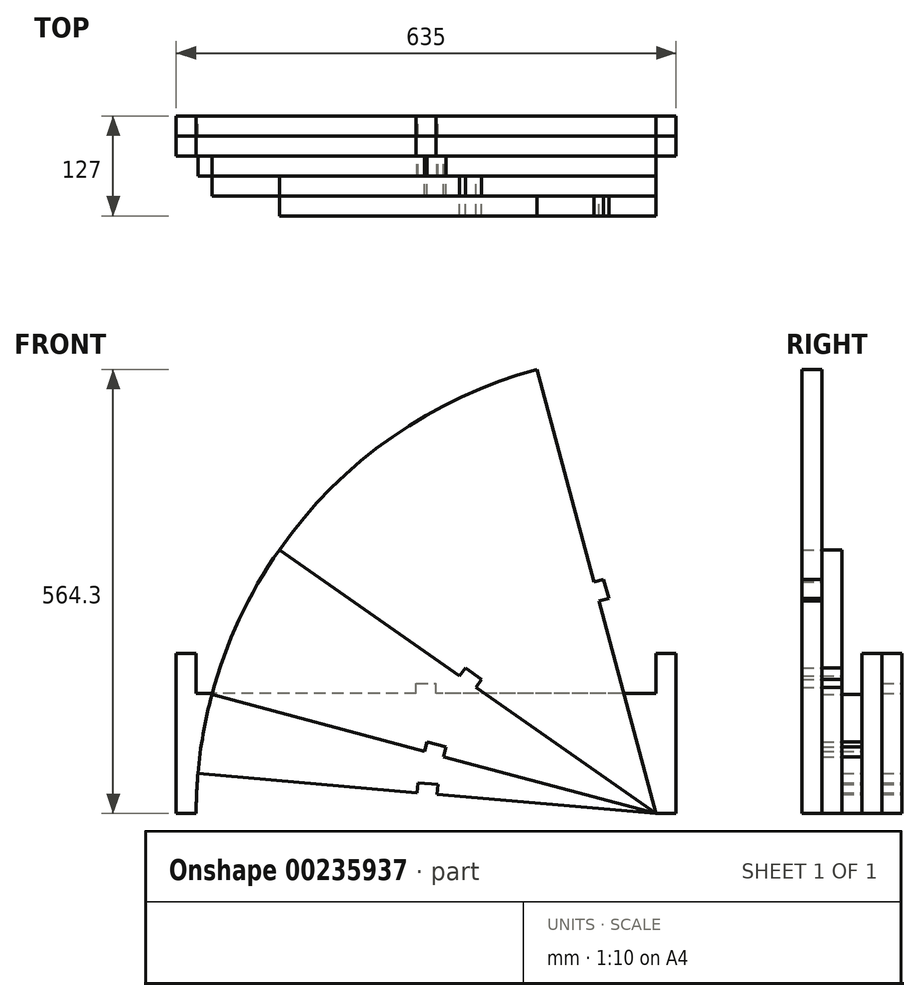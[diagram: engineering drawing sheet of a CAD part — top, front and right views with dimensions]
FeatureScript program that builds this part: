
annotation { "Feature Type Name" : "Feature", "Feature Type Description" : "" }
export const myFeature = defineFeature(function(context is Context, id is Id, definition is map)
    precondition{}
    {
        {
            var Q0;
            Q0=qCreatedBy(makeId("Front.planeOp"),FACE);
            var sketch = newSketch(context, id + "F0", { "sketchPlane" : qUnion([Q0])});
            skLineSegment(sketch, "E0", {"start": v(-127.48, -54.08) * mm, "end": v(177.32, -54.08) * mm});
            skLineSegment(sketch, "E1", {"start": v(507.52, -54.08) * mm, "end": v(507.52, 149.12) * mm});
            skLineSegment(sketch, "E2", {"start": v(507.52, 149.12) * mm, "end": v(482.12, 149.12) * mm});
            skLineSegment(sketch, "E3", {"start": v(482.12, 149.12) * mm, "end": v(482.12, 98.32) * mm});
            skLineSegment(sketch, "E4", {"start": v(482.12, 98.32) * mm, "end": v(202.72, 98.32) * mm});
            skLineSegment(sketch, "E5", {"start": v(-102.08, 98.32) * mm, "end": v(-102.08, 149.12) * mm});
            skLineSegment(sketch, "E6", {"start": v(-102.08, 149.12) * mm, "end": v(-127.48, 149.12) * mm});
            skLineSegment(sketch, "E7", {"start": v(-127.48, 149.12) * mm, "end": v(-127.48, -54.08) * mm});
            skPoint(sketch, "E8", {"position": v(190.02, 98.32) * mm});
            skPoint(sketch, "E9", {"position": v(202.72, 98.32) * mm});
            skPoint(sketch, "E10", {"position": v(177.32, 98.32) * mm});
            skLineSegment(sketch, "E11.top", {"start": v(177.32, 111.02) * mm, "end": v(202.72, 111.02) * mm});
            skLineSegment(sketch, "E11.left", {"start": v(177.32, 98.32) * mm, "end": v(177.32, 111.02) * mm});
            skLineSegment(sketch, "E11.right", {"start": v(202.72, 98.32) * mm, "end": v(202.72, 111.02) * mm});
            skLineSegment(sketch, "E12.trimOffspring", {"start": v(177.32, 98.32) * mm, "end": v(-102.08, 98.32) * mm});
            skArc(sketch, "E13", {"start": v(-102.08, -54.08) * mm, "mid": v(-101.52, -28.6) * mm, "end": v(-99.85, -3.16) * mm});
            skLineSegment(sketch, "E14", {"start": v(-99.85, -3.16) * mm, "end": v(178.48, -27.51) * mm});
            skLineSegment(sketch, "E15.top", {"start": v(202.72, -41.38) * mm, "end": v(177.32, -41.38) * mm});
            skLineSegment(sketch, "E15.left", {"start": v(202.72, -54.08) * mm, "end": v(202.72, -41.38) * mm});
            skLineSegment(sketch, "E15.right", {"start": v(177.32, -54.08) * mm, "end": v(177.32, -41.38) * mm});
            skLineSegment(sketch, "E16.trimOffspring", {"start": v(202.72, -54.08) * mm, "end": v(507.52, -54.08) * mm});
            skPoint(sketch, "E17", {"position": v(203.79, -29.73) * mm});
            skLineSegment(sketch, "E18", {"start": v(203.79, -29.73) * mm, "end": v(204.9, -17.07) * mm});
            skLineSegment(sketch, "E19", {"start": v(204.9, -17.07) * mm, "end": v(179.6, -14.86) * mm});
            skLineSegment(sketch, "E20", {"start": v(179.6, -14.86) * mm, "end": v(178.48, -27.51) * mm});
            skLineSegment(sketch, "E21.trimOffspring", {"start": v(203.79, -29.73) * mm, "end": v(482.12, -54.08) * mm});
            skSolve(sketch);
        }
        {
            var Q0;
            {var subQ4=sQuery(id+"F0.wireOp",EDGE,"E1");Q0=makeQuery(id+"F0.imprint","IMPRINT",FACE,{"disambiguationData":[TD([[makeQuery(id+"F0.imprint","IMPRINT",EDGE,{"derivedFrom":subQ4}),1.0]])]});}
            var Q1;
            {var subQ0=sQuery(id+"F0.wireOp",EDGE,"E13");Q1=makeQuery(id+"F0.imprint","IMPRINT",FACE,{"disambiguationData":[TD([[makeQuery(id+"F0.imprint","IMPRINT",EDGE,{"derivedFrom":subQ0}),-1.0]])]});}
            extrude(context, id + "F1", {"entities" : qUnion([Q0, Q1]), "depth" : 25.4 * mm});
        }
        {
            var Q0;
            {var subQ0=sQuery(id+"F0.wireOp",EDGE,"E13");Q0=makeQuery(id+"F0.imprint","IMPRINT",FACE,{"disambiguationData":[TD([[makeQuery(id+"F0.imprint","IMPRINT",EDGE,{"derivedFrom":subQ0}),-1.0]])]});}
            extrude(context, id + "F2", {"entities" : qUnion([Q0]), "depth" : 50.8 * mm});
        }
        {
            var Q0;
            Q0=makeQuery(id+"F2.opExtrude","CAP_FACE",FACE,{"disambiguationData":[OSD([sQuery(id+"F0.wireOp",EDGE,"E0"),sQuery(id+"F0.wireOp",EDGE,"E13"),sQuery(id+"F0.wireOp",EDGE,"E14"),sQuery(id+"F0.wireOp",EDGE,"E15.top"),sQuery(id+"F0.wireOp",EDGE,"E15.left"),sQuery(id+"F0.wireOp",EDGE,"E15.right"),sQuery(id+"F0.wireOp",EDGE,"E16.trimOffspring"),sQuery(id+"F0.wireOp",EDGE,"E18"),sQuery(id+"F0.wireOp",EDGE,"E19"),sQuery(id+"F0.wireOp",EDGE,"E20"),sQuery(id+"F0.wireOp",EDGE,"E21.trimOffspring")])],"isStart":false});
            var sketch = newSketch(context, id + "F3", { "sketchPlane" : qUnion([Q0])});
            skLineSegment(sketch, "E22.0", {"start": v(-99.85, -3.16) * mm, "end": v(178.48, -27.51) * mm});
            skLineSegment(sketch, "E23.0", {"start": v(203.79, -29.73) * mm, "end": v(482.12, -54.08) * mm});
            skLineSegment(sketch, "E24.0", {"start": v(204.9, -17.07) * mm, "end": v(179.6, -14.86) * mm});
            skLineSegment(sketch, "E25.0", {"start": v(179.6, -14.86) * mm, "end": v(178.48, -27.51) * mm});
            skLineSegment(sketch, "E26.0", {"start": v(203.79, -29.73) * mm, "end": v(204.9, -17.07) * mm});
            skArc(sketch, "E27", {"start": v(-99.85, -3.16) * mm, "mid": v(-93.2, 47.37) * mm, "end": v(-82.17, 97.13) * mm});
            skLineSegment(sketch, "E28", {"start": v(-82.17, 97.13) * mm, "end": v(187.71, 24.81) * mm});
            skPoint(sketch, "E29", {"position": v(212.25, 18.24) * mm});
            skLineSegment(sketch, "E30", {"start": v(212.25, 18.24) * mm, "end": v(215.53, 30.5) * mm});
            skLineSegment(sketch, "E31", {"start": v(215.53, 30.5) * mm, "end": v(191, 37.08) * mm});
            skLineSegment(sketch, "E32", {"start": v(191, 37.08) * mm, "end": v(187.71, 24.81) * mm});
            skLineSegment(sketch, "E33.trimOffspring", {"start": v(212.25, 18.24) * mm, "end": v(482.12, -54.08) * mm});
            skSolve(sketch);
        }
        {
            var Q0;
            Q0=makeQuery(id+"F3.imprint","IMPRINT",FACE,{"disambiguationData":[TD([[makeQuery(id+"F3.imprint","IMPRINT",EDGE,{"derivedFrom":sQuery(id+"F3.wireOp",EDGE,"E22.0")}),1.0]])]});
            extrude(context, id + "F4", {"entities" : qUnion([Q0]), "depth" : 25.4 * mm});
        }
        {
            var Q0;
            Q0=makeQuery(id+"F4.opExtrude","CAP_FACE",FACE,{"disambiguationData":[OSD([sQuery(id+"F3.wireOp",EDGE,"E22.0"),sQuery(id+"F3.wireOp",EDGE,"E23.0"),sQuery(id+"F3.wireOp",EDGE,"E24.0"),sQuery(id+"F3.wireOp",EDGE,"E25.0"),sQuery(id+"F3.wireOp",EDGE,"E26.0"),sQuery(id+"F3.wireOp",EDGE,"E27"),sQuery(id+"F3.wireOp",EDGE,"E28"),sQuery(id+"F3.wireOp",EDGE,"E30"),sQuery(id+"F3.wireOp",EDGE,"E31"),sQuery(id+"F3.wireOp",EDGE,"E32"),sQuery(id+"F3.wireOp",EDGE,"E33.trimOffspring")])],"isStart":false});
            var sketch = newSketch(context, id + "F5", { "sketchPlane" : qUnion([Q0])});
            skLineSegment(sketch, "E34.0", {"start": v(212.25, 18.24) * mm, "end": v(482.12, -54.08) * mm});
            skLineSegment(sketch, "E35.0", {"start": v(215.53, 30.5) * mm, "end": v(191, 37.08) * mm});
            skLineSegment(sketch, "E36.0", {"start": v(212.25, 18.24) * mm, "end": v(215.53, 30.5) * mm});
            skLineSegment(sketch, "E37.0", {"start": v(191, 37.08) * mm, "end": v(187.71, 24.81) * mm});
            skLineSegment(sketch, "E38.0", {"start": v(-82.17, 97.13) * mm, "end": v(187.71, 24.81) * mm});
            skArc(sketch, "E39", {"start": v(-82.17, 97.13) * mm, "mid": v(-47.34, 192.82) * mm, "end": v(3.58, 281) * mm});
            skLineSegment(sketch, "E40", {"start": v(3.58, 281) * mm, "end": v(232.45, 120.75) * mm});
            skPoint(sketch, "E41", {"position": v(253.25, 106.18) * mm});
            skPoint(sketch, "E42", {"position": v(232.45, 120.75) * mm});
            skLineSegment(sketch, "E43", {"start": v(253.25, 106.18) * mm, "end": v(260.54, 116.58) * mm});
            skLineSegment(sketch, "E44", {"start": v(232.45, 120.75) * mm, "end": v(239.73, 131.15) * mm});
            skLineSegment(sketch, "E45", {"start": v(239.73, 131.15) * mm, "end": v(260.54, 116.58) * mm});
            skLineSegment(sketch, "E46.trimOffspring", {"start": v(253.25, 106.18) * mm, "end": v(482.12, -54.08) * mm});
            skSolve(sketch);
        }
        {
            var Q0;
            Q0 = qSketchRegion(id + "F5", true);
            extrude(context, id + "F6", {"entities" : qUnion([Q0]), "depth" : 25.4 * mm});
        }
        {
            var Q0;
            Q0=makeQuery(id+"F6.opExtrude","CAP_FACE",FACE,{"disambiguationData":[OSD([sQuery(id+"F5.wireOp",EDGE,"E34.0"),sQuery(id+"F5.wireOp",EDGE,"E35.0"),sQuery(id+"F5.wireOp",EDGE,"E36.0"),sQuery(id+"F5.wireOp",EDGE,"E37.0"),sQuery(id+"F5.wireOp",EDGE,"E38.0"),sQuery(id+"F5.wireOp",EDGE,"E39"),sQuery(id+"F5.wireOp",EDGE,"E40"),sQuery(id+"F5.wireOp",EDGE,"E43"),sQuery(id+"F5.wireOp",EDGE,"E44"),sQuery(id+"F5.wireOp",EDGE,"E45"),sQuery(id+"F5.wireOp",EDGE,"E46.trimOffspring")])],"isStart":false});
            var sketch = newSketch(context, id + "F7", { "sketchPlane" : qUnion([Q0])});
            skLineSegment(sketch, "E47.0", {"start": v(239.73, 131.15) * mm, "end": v(260.54, 116.58) * mm});
            skLineSegment(sketch, "E48.0", {"start": v(3.58, 281) * mm, "end": v(232.45, 120.75) * mm});
            skLineSegment(sketch, "E49.0", {"start": v(232.45, 120.75) * mm, "end": v(239.73, 131.15) * mm});
            skLineSegment(sketch, "E50.0", {"start": v(253.25, 106.18) * mm, "end": v(482.12, -54.08) * mm});
            skLineSegment(sketch, "E51.0", {"start": v(253.25, 106.18) * mm, "end": v(260.54, 116.58) * mm});
            skArc(sketch, "E52", {"start": v(3.58, 281) * mm, "mid": v(147.04, 424.47) * mm, "end": v(330.92, 510.22) * mm});
            skLineSegment(sketch, "E53", {"start": v(330.92, 510.22) * mm, "end": v(403.24, 240.34) * mm});
            skLineSegment(sketch, "E54", {"start": v(403.24, 240.34) * mm, "end": v(415.5, 243.62) * mm});
            skLineSegment(sketch, "E55", {"start": v(415.5, 243.62) * mm, "end": v(422.08, 219.09) * mm});
            skLineSegment(sketch, "E56", {"start": v(422.08, 219.09) * mm, "end": v(409.81, 215.8) * mm});
            skLineSegment(sketch, "E57.trimOffspring", {"start": v(409.81, 215.8) * mm, "end": v(482.12, -54.08) * mm});
            skSolve(sketch);
        }
        {
            var Q0;
            Q0 = qSketchRegion(id + "F7", true);
            extrude(context, id + "F8", {"entities" : qUnion([Q0]), "depth" : 25.4 * mm});
        }
    });
